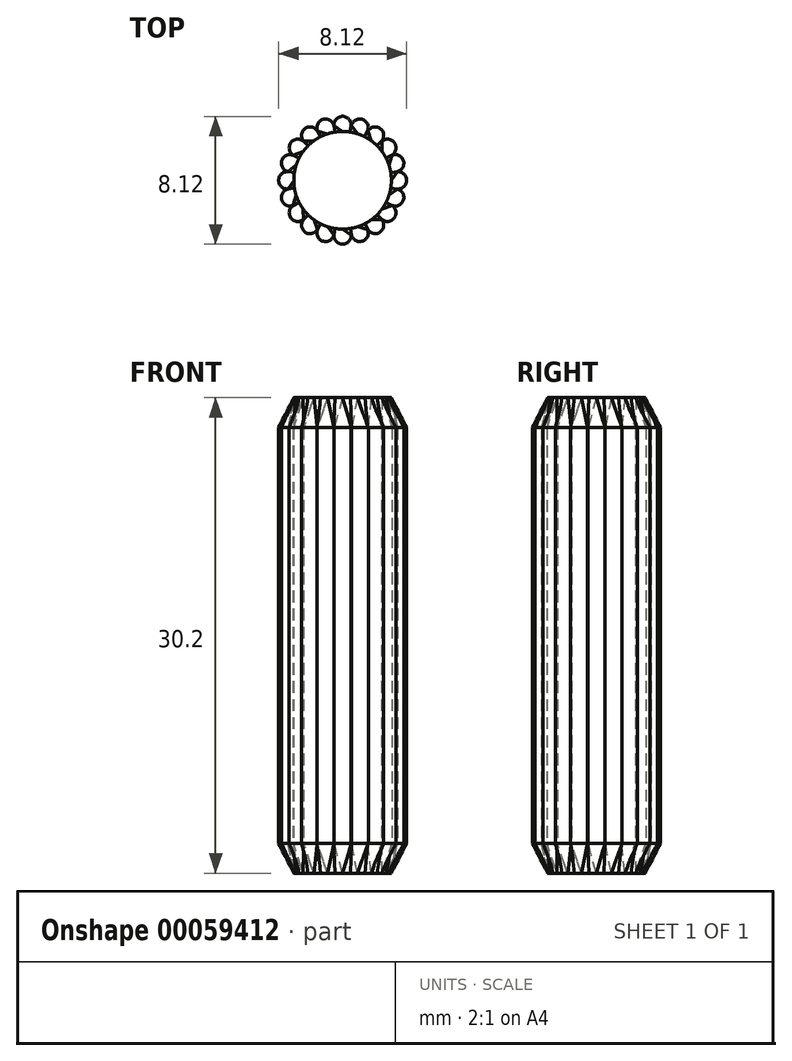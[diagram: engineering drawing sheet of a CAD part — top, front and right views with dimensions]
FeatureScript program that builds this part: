
annotation { "Feature Type Name" : "Feature", "Feature Type Description" : "" }
export const myFeature = defineFeature(function(context is Context, id is Id, definition is map)
    precondition{}
    {
        {
            var Q0;
            Q0=qCreatedBy(makeId("Top.planeOp"),FACE);
            var sketch = newSketch(context, id + "F0", { "sketchPlane" : qUnion([Q0])});
            skCircle(sketch, "E0", {"center": v(0, 3.52) * mm, "radius": 0.55 * mm});
            skCircle(sketch, "E1.1.0", {"center": v(-1.09, 3.35) * mm, "radius": 0.55 * mm});
            skCircle(sketch, "E1.2.0", {"center": v(-2.07, 2.85) * mm, "radius": 0.55 * mm});
            skCircle(sketch, "E1.3.0", {"center": v(-2.85, 2.07) * mm, "radius": 0.55 * mm});
            skCircle(sketch, "E1.4.0", {"center": v(-3.35, 1.09) * mm, "radius": 0.55 * mm});
            skCircle(sketch, "E1.5.0", {"center": v(-3.52, 0) * mm, "radius": 0.55 * mm});
            skCircle(sketch, "E1.6.0", {"center": v(-3.35, -1.09) * mm, "radius": 0.55 * mm});
            skCircle(sketch, "E1.7.0", {"center": v(-2.85, -2.07) * mm, "radius": 0.55 * mm});
            skCircle(sketch, "E1.8.0", {"center": v(-2.07, -2.85) * mm, "radius": 0.55 * mm});
            skCircle(sketch, "E1.9.0", {"center": v(-1.09, -3.35) * mm, "radius": 0.55 * mm});
            skCircle(sketch, "E1.10.0", {"center": v(0, -3.52) * mm, "radius": 0.55 * mm});
            skCircle(sketch, "E1.11.0", {"center": v(1.09, -3.35) * mm, "radius": 0.55 * mm});
            skCircle(sketch, "E1.12.0", {"center": v(2.07, -2.85) * mm, "radius": 0.55 * mm});
            skCircle(sketch, "E1.13.0", {"center": v(2.85, -2.07) * mm, "radius": 0.55 * mm});
            skCircle(sketch, "E1.14.0", {"center": v(3.35, -1.09) * mm, "radius": 0.55 * mm});
            skCircle(sketch, "E1.15.0", {"center": v(3.52, 0) * mm, "radius": 0.55 * mm});
            skCircle(sketch, "E1.16.0", {"center": v(3.35, 1.09) * mm, "radius": 0.55 * mm});
            skCircle(sketch, "E1.17.0", {"center": v(2.85, 2.07) * mm, "radius": 0.55 * mm});
            skCircle(sketch, "E1.18.0", {"center": v(2.07, 2.85) * mm, "radius": 0.55 * mm});
            skCircle(sketch, "E1.19.0", {"center": v(1.09, 3.35) * mm, "radius": 0.55 * mm});
            skPoint(sketch, "E1.center", {"position": v(0, 0) * mm});
            skCircle(sketch, "E2", {"center": v(0, 0) * mm, "radius": 3.52 * mm});
            skSolve(sketch);
        }
        {
            var Q0;
            {var subQ0=sQuery(id+"F0.wireOp",EDGE,"E2");var subQ1=sQuery(id+"F0.wireOp",EDGE,"E1.1.0");var subQ2=makeQuery(id+"F0.imprint","INTERSECT",VERTEX,{"disambiguationData":[OD(0.0)],"derivedFrom":[subQ1,subQ0]});Q0=makeQuery(id+"F0.imprint","IMPRINT",FACE,{"disambiguationData":[TD([[makeQuery(id+"F0.imprint","IMPRINT",EDGE,{"disambiguationData":[TD([[subQ2,-1.0]])],"derivedFrom":subQ1}),1.0]])]});}
            var Q1;
            {var subQ0=sQuery(id+"F0.wireOp",EDGE,"E2");var subQ1=sQuery(id+"F0.wireOp",EDGE,"E1.2.0");var subQ2=makeQuery(id+"F0.imprint","INTERSECT",VERTEX,{"disambiguationData":[OD(0.0)],"derivedFrom":[subQ1,subQ0]});Q1=makeQuery(id+"F0.imprint","IMPRINT",FACE,{"disambiguationData":[TD([[makeQuery(id+"F0.imprint","IMPRINT",EDGE,{"disambiguationData":[TD([[subQ2,-1.0]])],"derivedFrom":subQ1}),1.0]])]});}
            var Q2;
            {var subQ0=sQuery(id+"F0.wireOp",EDGE,"E2");var subQ1=sQuery(id+"F0.wireOp",EDGE,"E1.3.0");var subQ2=makeQuery(id+"F0.imprint","INTERSECT",VERTEX,{"disambiguationData":[OD(0.0)],"derivedFrom":[subQ1,subQ0]});Q2=makeQuery(id+"F0.imprint","IMPRINT",FACE,{"disambiguationData":[TD([[makeQuery(id+"F0.imprint","IMPRINT",EDGE,{"disambiguationData":[TD([[subQ2,-1.0]])],"derivedFrom":subQ1}),1.0]])]});}
            var Q3;
            {var subQ0=sQuery(id+"F0.wireOp",EDGE,"E2");var subQ1=sQuery(id+"F0.wireOp",EDGE,"E1.4.0");var subQ2=makeQuery(id+"F0.imprint","INTERSECT",VERTEX,{"disambiguationData":[OD(0.0)],"derivedFrom":[subQ1,subQ0]});Q3=makeQuery(id+"F0.imprint","IMPRINT",FACE,{"disambiguationData":[TD([[makeQuery(id+"F0.imprint","IMPRINT",EDGE,{"disambiguationData":[TD([[subQ2,-1.0]])],"derivedFrom":subQ1}),1.0]])]});}
            var Q4;
            {var subQ0=sQuery(id+"F0.wireOp",EDGE,"E2");var subQ18=sQuery(id+"F0.wireOp",EDGE,"E0");var subQ38=makeQuery(id+"F0.imprint","INTERSECT",VERTEX,{"disambiguationData":[OD(0.0)],"derivedFrom":[subQ18,subQ0]});Q4=makeQuery(id+"F0.imprint","IMPRINT",FACE,{"disambiguationData":[TD([[makeQuery(id+"F0.imprint","IMPRINT",EDGE,{"disambiguationData":[TD([[subQ38,1.0]])],"derivedFrom":subQ18}),-1.0]])]});}
            var Q5;
            {var subQ0=sQuery(id+"F0.wireOp",EDGE,"E2");var subQ1=sQuery(id+"F0.wireOp",EDGE,"E1.5.0");var subQ2=makeQuery(id+"F0.imprint","INTERSECT",VERTEX,{"disambiguationData":[OD(0.0)],"derivedFrom":[subQ1,subQ0]});Q5=makeQuery(id+"F0.imprint","IMPRINT",FACE,{"disambiguationData":[TD([[makeQuery(id+"F0.imprint","IMPRINT",EDGE,{"disambiguationData":[TD([[subQ2,-1.0]])],"derivedFrom":subQ1}),1.0]])]});}
            var Q6;
            {var subQ0=sQuery(id+"F0.wireOp",EDGE,"E2");var subQ1=sQuery(id+"F0.wireOp",EDGE,"E1.6.0");var subQ2=makeQuery(id+"F0.imprint","INTERSECT",VERTEX,{"disambiguationData":[OD(0.0)],"derivedFrom":[subQ1,subQ0]});Q6=makeQuery(id+"F0.imprint","IMPRINT",FACE,{"disambiguationData":[TD([[makeQuery(id+"F0.imprint","IMPRINT",EDGE,{"disambiguationData":[TD([[subQ2,-1.0]])],"derivedFrom":subQ1}),1.0]])]});}
            var Q7;
            {var subQ0=sQuery(id+"F0.wireOp",EDGE,"E2");var subQ1=sQuery(id+"F0.wireOp",EDGE,"E1.7.0");var subQ2=makeQuery(id+"F0.imprint","INTERSECT",VERTEX,{"disambiguationData":[OD(0.0)],"derivedFrom":[subQ1,subQ0]});Q7=makeQuery(id+"F0.imprint","IMPRINT",FACE,{"disambiguationData":[TD([[makeQuery(id+"F0.imprint","IMPRINT",EDGE,{"disambiguationData":[TD([[subQ2,-1.0]])],"derivedFrom":subQ1}),1.0]])]});}
            var Q8;
            {var subQ0=sQuery(id+"F0.wireOp",EDGE,"E2");var subQ1=sQuery(id+"F0.wireOp",EDGE,"E0");var subQ2=makeQuery(id+"F0.imprint","INTERSECT",VERTEX,{"disambiguationData":[OD(0.0)],"derivedFrom":[subQ1,subQ0]});Q8=makeQuery(id+"F0.imprint","IMPRINT",FACE,{"disambiguationData":[TD([[makeQuery(id+"F0.imprint","IMPRINT",EDGE,{"disambiguationData":[TD([[subQ2,-1.0]])],"derivedFrom":subQ1}),1.0]])]});}
            var Q9;
            {var subQ0=sQuery(id+"F0.wireOp",EDGE,"E2");var subQ1=sQuery(id+"F0.wireOp",EDGE,"E1.19.0");var subQ2=makeQuery(id+"F0.imprint","INTERSECT",VERTEX,{"disambiguationData":[OD(0.0)],"derivedFrom":[subQ1,subQ0]});Q9=makeQuery(id+"F0.imprint","IMPRINT",FACE,{"disambiguationData":[TD([[makeQuery(id+"F0.imprint","IMPRINT",EDGE,{"disambiguationData":[TD([[subQ2,-1.0]])],"derivedFrom":subQ1}),1.0]])]});}
            var Q10;
            {var subQ0=sQuery(id+"F0.wireOp",EDGE,"E2");var subQ1=sQuery(id+"F0.wireOp",EDGE,"E1.18.0");var subQ2=makeQuery(id+"F0.imprint","INTERSECT",VERTEX,{"disambiguationData":[OD(0.0)],"derivedFrom":[subQ1,subQ0]});Q10=makeQuery(id+"F0.imprint","IMPRINT",FACE,{"disambiguationData":[TD([[makeQuery(id+"F0.imprint","IMPRINT",EDGE,{"disambiguationData":[TD([[subQ2,-1.0]])],"derivedFrom":subQ1}),1.0]])]});}
            var Q11;
            {var subQ0=sQuery(id+"F0.wireOp",EDGE,"E2");var subQ1=sQuery(id+"F0.wireOp",EDGE,"E1.17.0");var subQ2=makeQuery(id+"F0.imprint","INTERSECT",VERTEX,{"disambiguationData":[OD(0.0)],"derivedFrom":[subQ1,subQ0]});Q11=makeQuery(id+"F0.imprint","IMPRINT",FACE,{"disambiguationData":[TD([[makeQuery(id+"F0.imprint","IMPRINT",EDGE,{"disambiguationData":[TD([[subQ2,-1.0]])],"derivedFrom":subQ1}),1.0]])]});}
            var Q12;
            {var subQ0=sQuery(id+"F0.wireOp",EDGE,"E2");var subQ1=sQuery(id+"F0.wireOp",EDGE,"E1.16.0");var subQ2=makeQuery(id+"F0.imprint","INTERSECT",VERTEX,{"disambiguationData":[OD(0.0)],"derivedFrom":[subQ1,subQ0]});Q12=makeQuery(id+"F0.imprint","IMPRINT",FACE,{"disambiguationData":[TD([[makeQuery(id+"F0.imprint","IMPRINT",EDGE,{"disambiguationData":[TD([[subQ2,-1.0]])],"derivedFrom":subQ1}),1.0]])]});}
            var Q13;
            {var subQ0=sQuery(id+"F0.wireOp",EDGE,"E2");var subQ1=sQuery(id+"F0.wireOp",EDGE,"E1.15.0");var subQ2=makeQuery(id+"F0.imprint","INTERSECT",VERTEX,{"disambiguationData":[OD(0.0)],"derivedFrom":[subQ1,subQ0]});Q13=makeQuery(id+"F0.imprint","IMPRINT",FACE,{"disambiguationData":[TD([[makeQuery(id+"F0.imprint","IMPRINT",EDGE,{"disambiguationData":[TD([[subQ2,1.0]])],"derivedFrom":subQ1}),1.0]])]});}
            var Q14;
            {var subQ0=sQuery(id+"F0.wireOp",EDGE,"E2");var subQ1=sQuery(id+"F0.wireOp",EDGE,"E1.14.0");var subQ2=makeQuery(id+"F0.imprint","INTERSECT",VERTEX,{"disambiguationData":[OD(0.0)],"derivedFrom":[subQ1,subQ0]});Q14=makeQuery(id+"F0.imprint","IMPRINT",FACE,{"disambiguationData":[TD([[makeQuery(id+"F0.imprint","IMPRINT",EDGE,{"disambiguationData":[TD([[subQ2,-1.0]])],"derivedFrom":subQ1}),1.0]])]});}
            var Q15;
            {var subQ0=sQuery(id+"F0.wireOp",EDGE,"E2");var subQ1=sQuery(id+"F0.wireOp",EDGE,"E1.13.0");var subQ2=makeQuery(id+"F0.imprint","INTERSECT",VERTEX,{"disambiguationData":[OD(0.0)],"derivedFrom":[subQ1,subQ0]});Q15=makeQuery(id+"F0.imprint","IMPRINT",FACE,{"disambiguationData":[TD([[makeQuery(id+"F0.imprint","IMPRINT",EDGE,{"disambiguationData":[TD([[subQ2,-1.0]])],"derivedFrom":subQ1}),1.0]])]});}
            var Q16;
            {var subQ0=sQuery(id+"F0.wireOp",EDGE,"E2");var subQ1=sQuery(id+"F0.wireOp",EDGE,"E1.12.0");var subQ2=makeQuery(id+"F0.imprint","INTERSECT",VERTEX,{"disambiguationData":[OD(0.0)],"derivedFrom":[subQ1,subQ0]});Q16=makeQuery(id+"F0.imprint","IMPRINT",FACE,{"disambiguationData":[TD([[makeQuery(id+"F0.imprint","IMPRINT",EDGE,{"disambiguationData":[TD([[subQ2,-1.0]])],"derivedFrom":subQ1}),1.0]])]});}
            var Q17;
            {var subQ0=sQuery(id+"F0.wireOp",EDGE,"E2");var subQ1=sQuery(id+"F0.wireOp",EDGE,"E1.11.0");var subQ2=makeQuery(id+"F0.imprint","INTERSECT",VERTEX,{"disambiguationData":[OD(0.0)],"derivedFrom":[subQ1,subQ0]});Q17=makeQuery(id+"F0.imprint","IMPRINT",FACE,{"disambiguationData":[TD([[makeQuery(id+"F0.imprint","IMPRINT",EDGE,{"disambiguationData":[TD([[subQ2,-1.0]])],"derivedFrom":subQ1}),1.0]])]});}
            var Q18;
            {var subQ0=sQuery(id+"F0.wireOp",EDGE,"E2");var subQ1=sQuery(id+"F0.wireOp",EDGE,"E1.10.0");var subQ2=makeQuery(id+"F0.imprint","INTERSECT",VERTEX,{"disambiguationData":[OD(0.0)],"derivedFrom":[subQ1,subQ0]});Q18=makeQuery(id+"F0.imprint","IMPRINT",FACE,{"disambiguationData":[TD([[makeQuery(id+"F0.imprint","IMPRINT",EDGE,{"disambiguationData":[TD([[subQ2,-1.0]])],"derivedFrom":subQ1}),1.0]])]});}
            var Q19;
            {var subQ0=sQuery(id+"F0.wireOp",EDGE,"E2");var subQ1=sQuery(id+"F0.wireOp",EDGE,"E1.9.0");var subQ2=makeQuery(id+"F0.imprint","INTERSECT",VERTEX,{"disambiguationData":[OD(0.0)],"derivedFrom":[subQ1,subQ0]});Q19=makeQuery(id+"F0.imprint","IMPRINT",FACE,{"disambiguationData":[TD([[makeQuery(id+"F0.imprint","IMPRINT",EDGE,{"disambiguationData":[TD([[subQ2,-1.0]])],"derivedFrom":subQ1}),1.0]])]});}
            var Q20;
            {var subQ0=sQuery(id+"F0.wireOp",EDGE,"E2");var subQ1=sQuery(id+"F0.wireOp",EDGE,"E1.8.0");var subQ2=makeQuery(id+"F0.imprint","INTERSECT",VERTEX,{"disambiguationData":[OD(0.0)],"derivedFrom":[subQ1,subQ0]});Q20=makeQuery(id+"F0.imprint","IMPRINT",FACE,{"disambiguationData":[TD([[makeQuery(id+"F0.imprint","IMPRINT",EDGE,{"disambiguationData":[TD([[subQ2,-1.0]])],"derivedFrom":subQ1}),1.0]])]});}
            var Q21;
            {var subQ0=sQuery(id+"F0.wireOp",EDGE,"E2");var subQ1=sQuery(id+"F0.wireOp",EDGE,"E1.8.0");var subQ2=makeQuery(id+"F0.imprint","INTERSECT",VERTEX,{"disambiguationData":[OD(0.0)],"derivedFrom":[subQ1,subQ0]});Q21=makeQuery(id+"F0.imprint","IMPRINT",FACE,{"disambiguationData":[TD([[makeQuery(id+"F0.imprint","IMPRINT",EDGE,{"disambiguationData":[TD([[subQ2,1.0]])],"derivedFrom":subQ1}),1.0]])]});}
            var Q22;
            {var subQ0=sQuery(id+"F0.wireOp",EDGE,"E2");var subQ1=sQuery(id+"F0.wireOp",EDGE,"E1.7.0");var subQ2=makeQuery(id+"F0.imprint","INTERSECT",VERTEX,{"disambiguationData":[OD(0.0)],"derivedFrom":[subQ1,subQ0]});Q22=makeQuery(id+"F0.imprint","IMPRINT",FACE,{"disambiguationData":[TD([[makeQuery(id+"F0.imprint","IMPRINT",EDGE,{"disambiguationData":[TD([[subQ2,1.0]])],"derivedFrom":subQ1}),1.0]])]});}
            var Q23;
            {var subQ0=sQuery(id+"F0.wireOp",EDGE,"E2");var subQ1=sQuery(id+"F0.wireOp",EDGE,"E1.6.0");var subQ2=makeQuery(id+"F0.imprint","INTERSECT",VERTEX,{"disambiguationData":[OD(0.0)],"derivedFrom":[subQ1,subQ0]});Q23=makeQuery(id+"F0.imprint","IMPRINT",FACE,{"disambiguationData":[TD([[makeQuery(id+"F0.imprint","IMPRINT",EDGE,{"disambiguationData":[TD([[subQ2,1.0]])],"derivedFrom":subQ1}),1.0]])]});}
            var Q24;
            {var subQ0=sQuery(id+"F0.wireOp",EDGE,"E2");var subQ1=sQuery(id+"F0.wireOp",EDGE,"E1.5.0");var subQ2=makeQuery(id+"F0.imprint","INTERSECT",VERTEX,{"disambiguationData":[OD(0.0)],"derivedFrom":[subQ1,subQ0]});Q24=makeQuery(id+"F0.imprint","IMPRINT",FACE,{"disambiguationData":[TD([[makeQuery(id+"F0.imprint","IMPRINT",EDGE,{"disambiguationData":[TD([[subQ2,1.0]])],"derivedFrom":subQ1}),1.0]])]});}
            var Q25;
            {var subQ0=sQuery(id+"F0.wireOp",EDGE,"E2");var subQ1=sQuery(id+"F0.wireOp",EDGE,"E1.4.0");var subQ2=makeQuery(id+"F0.imprint","INTERSECT",VERTEX,{"disambiguationData":[OD(0.0)],"derivedFrom":[subQ1,subQ0]});Q25=makeQuery(id+"F0.imprint","IMPRINT",FACE,{"disambiguationData":[TD([[makeQuery(id+"F0.imprint","IMPRINT",EDGE,{"disambiguationData":[TD([[subQ2,1.0]])],"derivedFrom":subQ1}),1.0]])]});}
            var Q26;
            {var subQ0=sQuery(id+"F0.wireOp",EDGE,"E2");var subQ1=sQuery(id+"F0.wireOp",EDGE,"E1.3.0");var subQ2=makeQuery(id+"F0.imprint","INTERSECT",VERTEX,{"disambiguationData":[OD(0.0)],"derivedFrom":[subQ1,subQ0]});Q26=makeQuery(id+"F0.imprint","IMPRINT",FACE,{"disambiguationData":[TD([[makeQuery(id+"F0.imprint","IMPRINT",EDGE,{"disambiguationData":[TD([[subQ2,1.0]])],"derivedFrom":subQ1}),1.0]])]});}
            var Q27;
            {var subQ0=sQuery(id+"F0.wireOp",EDGE,"E2");var subQ1=sQuery(id+"F0.wireOp",EDGE,"E1.2.0");var subQ2=makeQuery(id+"F0.imprint","INTERSECT",VERTEX,{"disambiguationData":[OD(0.0)],"derivedFrom":[subQ1,subQ0]});Q27=makeQuery(id+"F0.imprint","IMPRINT",FACE,{"disambiguationData":[TD([[makeQuery(id+"F0.imprint","IMPRINT",EDGE,{"disambiguationData":[TD([[subQ2,1.0]])],"derivedFrom":subQ1}),1.0]])]});}
            var Q28;
            {var subQ0=sQuery(id+"F0.wireOp",EDGE,"E2");var subQ1=sQuery(id+"F0.wireOp",EDGE,"E1.1.0");var subQ2=makeQuery(id+"F0.imprint","INTERSECT",VERTEX,{"disambiguationData":[OD(0.0)],"derivedFrom":[subQ1,subQ0]});Q28=makeQuery(id+"F0.imprint","IMPRINT",FACE,{"disambiguationData":[TD([[makeQuery(id+"F0.imprint","IMPRINT",EDGE,{"disambiguationData":[TD([[subQ2,1.0]])],"derivedFrom":subQ1}),1.0]])]});}
            var Q29;
            {var subQ0=sQuery(id+"F0.wireOp",EDGE,"E2");var subQ1=sQuery(id+"F0.wireOp",EDGE,"E0");var subQ2=makeQuery(id+"F0.imprint","INTERSECT",VERTEX,{"disambiguationData":[OD(0.0)],"derivedFrom":[subQ1,subQ0]});Q29=makeQuery(id+"F0.imprint","IMPRINT",FACE,{"disambiguationData":[TD([[makeQuery(id+"F0.imprint","IMPRINT",EDGE,{"disambiguationData":[TD([[subQ2,1.0]])],"derivedFrom":subQ1}),1.0]])]});}
            var Q30;
            {var subQ0=sQuery(id+"F0.wireOp",EDGE,"E2");var subQ1=sQuery(id+"F0.wireOp",EDGE,"E1.19.0");var subQ2=makeQuery(id+"F0.imprint","INTERSECT",VERTEX,{"disambiguationData":[OD(0.0)],"derivedFrom":[subQ1,subQ0]});Q30=makeQuery(id+"F0.imprint","IMPRINT",FACE,{"disambiguationData":[TD([[makeQuery(id+"F0.imprint","IMPRINT",EDGE,{"disambiguationData":[TD([[subQ2,1.0]])],"derivedFrom":subQ1}),1.0]])]});}
            var Q31;
            {var subQ0=sQuery(id+"F0.wireOp",EDGE,"E2");var subQ1=sQuery(id+"F0.wireOp",EDGE,"E1.18.0");var subQ2=makeQuery(id+"F0.imprint","INTERSECT",VERTEX,{"disambiguationData":[OD(0.0)],"derivedFrom":[subQ1,subQ0]});Q31=makeQuery(id+"F0.imprint","IMPRINT",FACE,{"disambiguationData":[TD([[makeQuery(id+"F0.imprint","IMPRINT",EDGE,{"disambiguationData":[TD([[subQ2,1.0]])],"derivedFrom":subQ1}),1.0]])]});}
            var Q32;
            {var subQ0=sQuery(id+"F0.wireOp",EDGE,"E2");var subQ1=sQuery(id+"F0.wireOp",EDGE,"E1.17.0");var subQ2=makeQuery(id+"F0.imprint","INTERSECT",VERTEX,{"disambiguationData":[OD(0.0)],"derivedFrom":[subQ1,subQ0]});Q32=makeQuery(id+"F0.imprint","IMPRINT",FACE,{"disambiguationData":[TD([[makeQuery(id+"F0.imprint","IMPRINT",EDGE,{"disambiguationData":[TD([[subQ2,1.0]])],"derivedFrom":subQ1}),1.0]])]});}
            var Q33;
            {var subQ0=sQuery(id+"F0.wireOp",EDGE,"E2");var subQ1=sQuery(id+"F0.wireOp",EDGE,"E1.16.0");var subQ2=makeQuery(id+"F0.imprint","INTERSECT",VERTEX,{"disambiguationData":[OD(0.0)],"derivedFrom":[subQ1,subQ0]});Q33=makeQuery(id+"F0.imprint","IMPRINT",FACE,{"disambiguationData":[TD([[makeQuery(id+"F0.imprint","IMPRINT",EDGE,{"disambiguationData":[TD([[subQ2,1.0]])],"derivedFrom":subQ1}),1.0]])]});}
            var Q34;
            {var subQ0=sQuery(id+"F0.wireOp",EDGE,"E2");var subQ1=sQuery(id+"F0.wireOp",EDGE,"E1.15.0");var subQ2=makeQuery(id+"F0.imprint","INTERSECT",VERTEX,{"disambiguationData":[OD(0.0)],"derivedFrom":[subQ1,subQ0]});Q34=makeQuery(id+"F0.imprint","IMPRINT",FACE,{"disambiguationData":[TD([[makeQuery(id+"F0.imprint","IMPRINT",EDGE,{"disambiguationData":[TD([[subQ2,-1.0]])],"derivedFrom":subQ1}),1.0]])]});}
            var Q35;
            {var subQ0=sQuery(id+"F0.wireOp",EDGE,"E2");var subQ1=sQuery(id+"F0.wireOp",EDGE,"E1.14.0");var subQ2=makeQuery(id+"F0.imprint","INTERSECT",VERTEX,{"disambiguationData":[OD(0.0)],"derivedFrom":[subQ1,subQ0]});Q35=makeQuery(id+"F0.imprint","IMPRINT",FACE,{"disambiguationData":[TD([[makeQuery(id+"F0.imprint","IMPRINT",EDGE,{"disambiguationData":[TD([[subQ2,1.0]])],"derivedFrom":subQ1}),1.0]])]});}
            var Q36;
            {var subQ0=sQuery(id+"F0.wireOp",EDGE,"E2");var subQ1=sQuery(id+"F0.wireOp",EDGE,"E1.13.0");var subQ2=makeQuery(id+"F0.imprint","INTERSECT",VERTEX,{"disambiguationData":[OD(0.0)],"derivedFrom":[subQ1,subQ0]});Q36=makeQuery(id+"F0.imprint","IMPRINT",FACE,{"disambiguationData":[TD([[makeQuery(id+"F0.imprint","IMPRINT",EDGE,{"disambiguationData":[TD([[subQ2,1.0]])],"derivedFrom":subQ1}),1.0]])]});}
            var Q37;
            {var subQ0=sQuery(id+"F0.wireOp",EDGE,"E2");var subQ1=sQuery(id+"F0.wireOp",EDGE,"E1.12.0");var subQ2=makeQuery(id+"F0.imprint","INTERSECT",VERTEX,{"disambiguationData":[OD(0.0)],"derivedFrom":[subQ1,subQ0]});Q37=makeQuery(id+"F0.imprint","IMPRINT",FACE,{"disambiguationData":[TD([[makeQuery(id+"F0.imprint","IMPRINT",EDGE,{"disambiguationData":[TD([[subQ2,1.0]])],"derivedFrom":subQ1}),1.0]])]});}
            var Q38;
            {var subQ0=sQuery(id+"F0.wireOp",EDGE,"E2");var subQ1=sQuery(id+"F0.wireOp",EDGE,"E1.11.0");var subQ2=makeQuery(id+"F0.imprint","INTERSECT",VERTEX,{"disambiguationData":[OD(0.0)],"derivedFrom":[subQ1,subQ0]});Q38=makeQuery(id+"F0.imprint","IMPRINT",FACE,{"disambiguationData":[TD([[makeQuery(id+"F0.imprint","IMPRINT",EDGE,{"disambiguationData":[TD([[subQ2,1.0]])],"derivedFrom":subQ1}),1.0]])]});}
            var Q39;
            {var subQ0=sQuery(id+"F0.wireOp",EDGE,"E2");var subQ1=sQuery(id+"F0.wireOp",EDGE,"E1.10.0");var subQ2=makeQuery(id+"F0.imprint","INTERSECT",VERTEX,{"disambiguationData":[OD(0.0)],"derivedFrom":[subQ1,subQ0]});Q39=makeQuery(id+"F0.imprint","IMPRINT",FACE,{"disambiguationData":[TD([[makeQuery(id+"F0.imprint","IMPRINT",EDGE,{"disambiguationData":[TD([[subQ2,1.0]])],"derivedFrom":subQ1}),1.0]])]});}
            var Q40;
            {var subQ0=sQuery(id+"F0.wireOp",EDGE,"E2");var subQ1=sQuery(id+"F0.wireOp",EDGE,"E1.9.0");var subQ2=makeQuery(id+"F0.imprint","INTERSECT",VERTEX,{"disambiguationData":[OD(0.0)],"derivedFrom":[subQ1,subQ0]});Q40=makeQuery(id+"F0.imprint","IMPRINT",FACE,{"disambiguationData":[TD([[makeQuery(id+"F0.imprint","IMPRINT",EDGE,{"disambiguationData":[TD([[subQ2,1.0]])],"derivedFrom":subQ1}),1.0]])]});}
            extrude(context, id + "F1", {"entities" : qUnion([Q0, Q1, Q2, Q3, Q4, Q5, Q6, Q7, Q8, Q9, Q10, Q11, Q12, Q13, Q14, Q15, Q16, Q17, Q18, Q19, Q20, Q21, Q22, Q23, Q24, Q25, Q26, Q27, Q28, Q29, Q30, Q31, Q32, Q33, Q34, Q35, Q36, Q37, Q38, Q39, Q40]), "depth" : 26.4 * mm});
        }
        {
            var Q0;
            Q0=makeQuery(id+"F1.opExtrude","CAP_FACE",FACE,{"disambiguationData":[OSD([sQuery(id+"F0.wireOp",EDGE,"E0"),sQuery(id+"F0.wireOp",EDGE,"E1.1.0"),sQuery(id+"F0.wireOp",EDGE,"E1.2.0"),sQuery(id+"F0.wireOp",EDGE,"E1.3.0"),sQuery(id+"F0.wireOp",EDGE,"E1.4.0"),sQuery(id+"F0.wireOp",EDGE,"E1.5.0"),sQuery(id+"F0.wireOp",EDGE,"E1.6.0"),sQuery(id+"F0.wireOp",EDGE,"E1.7.0"),sQuery(id+"F0.wireOp",EDGE,"E1.8.0"),sQuery(id+"F0.wireOp",EDGE,"E1.9.0"),sQuery(id+"F0.wireOp",EDGE,"E1.10.0"),sQuery(id+"F0.wireOp",EDGE,"E1.11.0"),sQuery(id+"F0.wireOp",EDGE,"E1.12.0"),sQuery(id+"F0.wireOp",EDGE,"E1.13.0"),sQuery(id+"F0.wireOp",EDGE,"E1.14.0"),sQuery(id+"F0.wireOp",EDGE,"E1.15.0"),sQuery(id+"F0.wireOp",EDGE,"E1.16.0"),sQuery(id+"F0.wireOp",EDGE,"E1.17.0"),sQuery(id+"F0.wireOp",EDGE,"E1.18.0"),sQuery(id+"F0.wireOp",EDGE,"E1.19.0"),sQuery(id+"F0.wireOp",EDGE,"E2")])],"isStart":false});
            cPlane(context, id + "F2", {"entities" : qUnion([Q0]), "cplaneType" : CPlaneType.OFFSET, "offset" : 1.9 * mm, "width" : 152.4 * mm, "height" : 152.4 * mm});
        }
        {
            var Q0;
            Q0=qCreatedBy(id+"F2.planeOp",FACE);
            var sketch = newSketch(context, id + "F3", { "sketchPlane" : qUnion([Q0])});
            skCircle(sketch, "E3", {"center": v(0, 0) * mm, "radius": 3.1 * mm});
            skSolve(sketch);
        }
        {
            var Q1;
            Q1=makeQuery(id+"F3.imprint","IMPRINT",FACE,{"disambiguationData":[TD([[makeQuery(id+"F3.imprint","IMPRINT",EDGE,{"derivedFrom":sQuery(id+"F3.wireOp",EDGE,"E3")}),1.0]])]});
            var Q2;
            Q2=makeQuery(id+"F1.opExtrude","CAP_FACE",FACE,{"disambiguationData":[OSD([sQuery(id+"F0.wireOp",EDGE,"E0"),sQuery(id+"F0.wireOp",EDGE,"E1.1.0"),sQuery(id+"F0.wireOp",EDGE,"E1.2.0"),sQuery(id+"F0.wireOp",EDGE,"E1.3.0"),sQuery(id+"F0.wireOp",EDGE,"E1.4.0"),sQuery(id+"F0.wireOp",EDGE,"E1.5.0"),sQuery(id+"F0.wireOp",EDGE,"E1.6.0"),sQuery(id+"F0.wireOp",EDGE,"E1.7.0"),sQuery(id+"F0.wireOp",EDGE,"E1.8.0"),sQuery(id+"F0.wireOp",EDGE,"E1.9.0"),sQuery(id+"F0.wireOp",EDGE,"E1.10.0"),sQuery(id+"F0.wireOp",EDGE,"E1.11.0"),sQuery(id+"F0.wireOp",EDGE,"E1.12.0"),sQuery(id+"F0.wireOp",EDGE,"E1.13.0"),sQuery(id+"F0.wireOp",EDGE,"E1.14.0"),sQuery(id+"F0.wireOp",EDGE,"E1.15.0"),sQuery(id+"F0.wireOp",EDGE,"E1.16.0"),sQuery(id+"F0.wireOp",EDGE,"E1.17.0"),sQuery(id+"F0.wireOp",EDGE,"E1.18.0"),sQuery(id+"F0.wireOp",EDGE,"E1.19.0"),sQuery(id+"F0.wireOp",EDGE,"E2")])],"isStart":false});
            loft(context, id + "F4", {"operationType" : NewBodyOperationType.ADD, "sheetProfilesArray" : [{ "sheetProfileEntities" : qUnion([Q1]) }, { "sheetProfileEntities" : qUnion([Q2]) }]});
        }
        {
            var Q0;
            Q0=makeQuery(id+"F1.opExtrude","CAP_FACE",FACE,{"disambiguationData":[OSD([sQuery(id+"F0.wireOp",EDGE,"E0"),sQuery(id+"F0.wireOp",EDGE,"E1.1.0"),sQuery(id+"F0.wireOp",EDGE,"E1.2.0"),sQuery(id+"F0.wireOp",EDGE,"E1.3.0"),sQuery(id+"F0.wireOp",EDGE,"E1.4.0"),sQuery(id+"F0.wireOp",EDGE,"E1.5.0"),sQuery(id+"F0.wireOp",EDGE,"E1.6.0"),sQuery(id+"F0.wireOp",EDGE,"E1.7.0"),sQuery(id+"F0.wireOp",EDGE,"E1.8.0"),sQuery(id+"F0.wireOp",EDGE,"E1.9.0"),sQuery(id+"F0.wireOp",EDGE,"E1.10.0"),sQuery(id+"F0.wireOp",EDGE,"E1.11.0"),sQuery(id+"F0.wireOp",EDGE,"E1.12.0"),sQuery(id+"F0.wireOp",EDGE,"E1.13.0"),sQuery(id+"F0.wireOp",EDGE,"E1.14.0"),sQuery(id+"F0.wireOp",EDGE,"E1.15.0"),sQuery(id+"F0.wireOp",EDGE,"E1.16.0"),sQuery(id+"F0.wireOp",EDGE,"E1.17.0"),sQuery(id+"F0.wireOp",EDGE,"E1.18.0"),sQuery(id+"F0.wireOp",EDGE,"E1.19.0"),sQuery(id+"F0.wireOp",EDGE,"E2")])],"isStart":true});
            cPlane(context, id + "F5", {"entities" : qUnion([Q0]), "cplaneType" : CPlaneType.OFFSET, "offset" : 1.9 * mm, "width" : 152.4 * mm, "height" : 152.4 * mm});
        }
        {
            var Q0;
            Q0=qCreatedBy(id+"F5.planeOp",FACE);
            var sketch = newSketch(context, id + "F6", { "sketchPlane" : qUnion([Q0])});
            skCircle(sketch, "E4", {"center": v(0, 0) * mm, "radius": 3.1 * mm});
            skSolve(sketch);
        }
        {
            var Q1;
            Q1=makeQuery(id+"F6.imprint","IMPRINT",FACE,{"disambiguationData":[TD([[makeQuery(id+"F6.imprint","IMPRINT",EDGE,{"derivedFrom":sQuery(id+"F6.wireOp",EDGE,"E4")}),1.0]])]});
            var Q2;
            Q2=makeQuery(id+"F1.opExtrude","CAP_FACE",FACE,{"disambiguationData":[OSD([sQuery(id+"F0.wireOp",EDGE,"E0"),sQuery(id+"F0.wireOp",EDGE,"E1.1.0"),sQuery(id+"F0.wireOp",EDGE,"E1.2.0"),sQuery(id+"F0.wireOp",EDGE,"E1.3.0"),sQuery(id+"F0.wireOp",EDGE,"E1.4.0"),sQuery(id+"F0.wireOp",EDGE,"E1.5.0"),sQuery(id+"F0.wireOp",EDGE,"E1.6.0"),sQuery(id+"F0.wireOp",EDGE,"E1.7.0"),sQuery(id+"F0.wireOp",EDGE,"E1.8.0"),sQuery(id+"F0.wireOp",EDGE,"E1.9.0"),sQuery(id+"F0.wireOp",EDGE,"E1.10.0"),sQuery(id+"F0.wireOp",EDGE,"E1.11.0"),sQuery(id+"F0.wireOp",EDGE,"E1.12.0"),sQuery(id+"F0.wireOp",EDGE,"E1.13.0"),sQuery(id+"F0.wireOp",EDGE,"E1.14.0"),sQuery(id+"F0.wireOp",EDGE,"E1.15.0"),sQuery(id+"F0.wireOp",EDGE,"E1.16.0"),sQuery(id+"F0.wireOp",EDGE,"E1.17.0"),sQuery(id+"F0.wireOp",EDGE,"E1.18.0"),sQuery(id+"F0.wireOp",EDGE,"E1.19.0"),sQuery(id+"F0.wireOp",EDGE,"E2")])],"isStart":true});
            loft(context, id + "F7", {"operationType" : NewBodyOperationType.ADD, "sheetProfilesArray" : [{ "sheetProfileEntities" : qUnion([Q1]) }, { "sheetProfileEntities" : qUnion([Q2]) }]});
        }
    });
